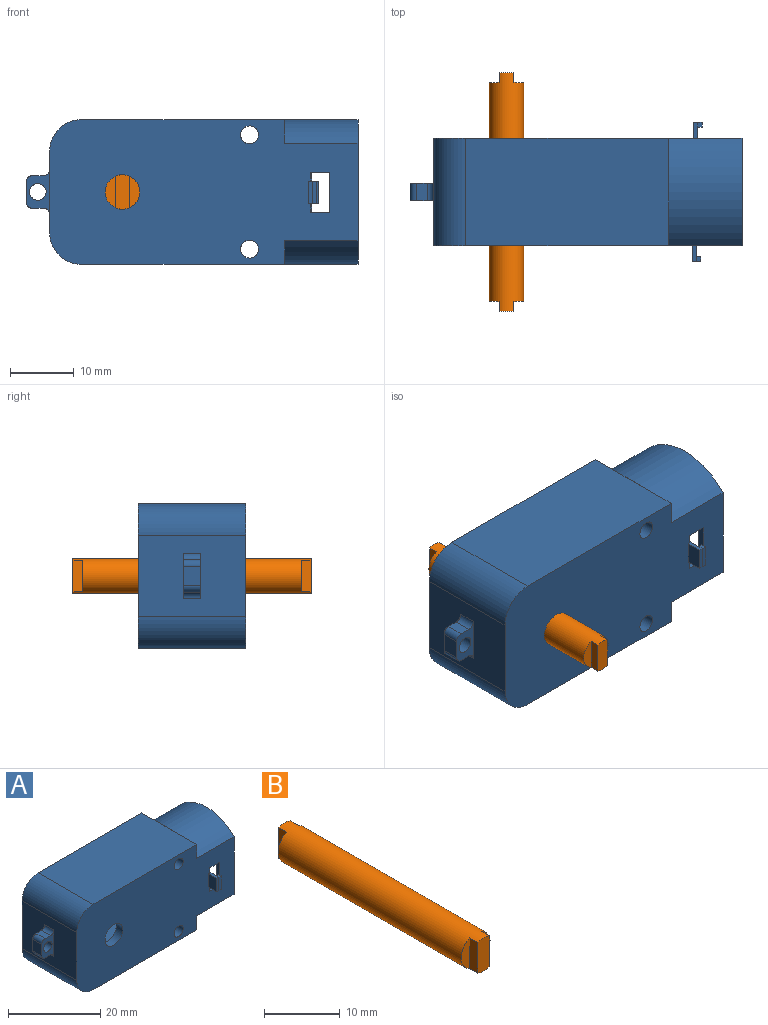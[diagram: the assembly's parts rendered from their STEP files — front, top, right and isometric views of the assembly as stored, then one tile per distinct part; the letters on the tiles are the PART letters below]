
ASSEMBLY  parts=2 mates=1
PART A: 73 faces, bbox 52x21.8x22.7 mm
  f0: plane 48.3x22.7mm, normal (0,-1,0), area 944.9mm2, adj f5,f8,f10,f11,f12,f13,f14,f15
  f1: plane 48.3x22.7mm, normal (0,1,0), area 944.9mm2, adj f6,f7,f8,f9,f10,f11,f12,f15
  f2: plane 14.47x11.5mm, normal (0,-1,0), area 148.7mm2, adj f4,f26,f27,f29,f38,f39,f40,f41
  f3: plane 14.47x11.5mm, normal (0,1,0), area 148.7mm2, adj f4,f26,f27,f29,f30,f31,f32,f33
  f4: plane 20.7x14.8mm, normal (1,0,0), area 254mm2, adj f2,f3,f24,f26,f27
  f5: plane 8.4x3.72mm, normal (1,0,0), area 9.6mm2, adj f0,f12,f28
  f6: plane 8.4x3.72mm, normal (1,0,0), area 9.6mm2, adj f1,f12,f28
  f7: plane 8.4x3.72mm, normal (1,0,0), area 9.6mm2, adj f1,f10,f25
  f8: cylinder r=1.4mm len=16.8mm, axis (0,1,0), area 81.1mm2, adj f0,f1,f16,f18,f22,f23
  f9: cylinder r=2.7mm len=5.4mm, axis (0,1,0), area 33.9mm2, adj f1,f23
  f10: plane 31.8x16.8mm, normal (0,0,1), area 534.2mm2, adj f0,f1,f7,f14,f67
  f11: plane 16.8x12.7mm, normal (-1,0,0), area 193.5mm2, adj f0,f1,f61,f63,f67,f68,f69,f70
  f12: plane 31.8x16.8mm, normal (0,0,-1), area 534.2mm2, adj f0,f1,f5,f6,f68
  f13: cylinder r=2.7mm len=5.4mm, axis (0,1,0), area 33.9mm2, adj f0,f22
  f14: plane 8.4x3.72mm, normal (1,0,0), area 9.6mm2, adj f0,f10,f25
  f15: cylinder r=1.4mm len=16.8mm, axis (0,1,0), area 81.1mm2, adj f0,f1,f17,f20,f22,f23
  f16: plane 27.96x12.8mm, normal (0,0,-1), area 357.9mm2, adj f8,f19,f22,f23
  f17: plane 27.96x12.8mm, normal (0,0,1), area 357.9mm2, adj f15,f19,f22,f23
  f18: plane 12.8x2.16mm, normal (0,0,-1), area 27.6mm2, adj f8,f21,f22,f23
  f19: plane 18.7x12.8mm, normal (1,0,0), area 239.4mm2, adj f16,f17,f22,f23
  f20: plane 12.8x2.16mm, normal (0,0,1), area 27.6mm2, adj f15,f21,f22,f23
  f21: plane 18.7x12.8mm, normal (-1,0,0), area 215.6mm2, adj f18,f20,f22,f23,f24
  f22: plane 32.8x18.7mm, normal (0,1,0), area 582.1mm2, adj f8,f13,f15,f16,f17,f18,f19,f20
  f23: plane 32.8x18.7mm, normal (0,-1,0), area 582.1mm2, adj f8,f9,f15,f16,f17,f18,f19,f20
  f24: cylinder r=2.75mm len=5.5mm, axis (1,0,0), area 34.6mm2, adj f4,f21
  f25: cylinder r=11.35mm len=16.8mm, axis (-1,0,0), area 217.5mm2, adj f0,f1,f7,f14,f29
  f26: cylinder r=10.35mm len=14.8mm, axis (-1,0,0), area 189.6mm2, adj f2,f3,f4,f29
  f27: cylinder r=10.35mm len=14.8mm, axis (-1,0,0), area 189.6mm2, adj f2,f3,f4,f29
  f28: cylinder r=11.35mm len=16.8mm, axis (-1,0,0), area 217.5mm2, adj f0,f1,f5,f6,f29
  f29: plane 22.7x16.8mm, normal (1,0,0), area 65.1mm2, adj f0,f1,f2,f3,f25,f26,f27,f28
  f30: plane 3.51x0.66mm, normal (0,0,1), area 1.9mm2, adj f0,f3,f31,f37,f54,f55,f59
  f31: plane 3.5x2.72mm, normal (1,0,0), area 9.5mm2, adj f3,f30,f32,f58
  f32: plane 3.51x0.66mm, normal (0,0,-1), area 1.9mm2, adj f0,f3,f31,f33,f54,f55,f57
  f33: plane 1.4x1mm, normal (1,0,0), area 1.4mm2, adj f0,f3,f32,f34
  f34: plane 3x1mm, normal (0,0,1), area 3mm2, adj f0,f3,f33,f35
  f35: plane 6.3x1mm, normal (-1,0,0), area 6.3mm2, adj f0,f3,f34,f36
  f36: plane 3x1mm, normal (0,0,-1), area 3mm2, adj f0,f3,f35,f37
  f37: plane 1.4x1mm, normal (1,0,0), area 1.4mm2, adj f0,f3,f30,f36
  f38: plane 3.51x0.65mm, normal (0,0,1), area 1.9mm2, adj f1,f2,f39,f45,f46,f47,f50
  f39: plane 1.4x1mm, normal (1,0,0), area 1.4mm2, adj f1,f2,f38,f40
  f40: plane 3x1mm, normal (0,0,-1), area 3mm2, adj f1,f2,f39,f41
  f41: plane 6.3x1mm, normal (-1,0,0), area 6.3mm2, adj f1,f2,f40,f42
  f42: plane 3x1mm, normal (0,0,1), area 3mm2, adj f1,f2,f41,f43
  f43: plane 1.4x1mm, normal (1,0,0), area 1.4mm2, adj f1,f2,f42,f44
  f44: plane 3.5x0.65mm, normal (0,0,-1), area 1.9mm2, adj f1,f2,f43,f45,f46,f47,f52
  f45: plane 3.5x2.72mm, normal (1,0,0), area 9.5mm2, adj f2,f38,f44,f51
  f46: plane 3.5x2.5mm, normal (-1,0,0), area 8.8mm2, adj f1,f38,f44,f47
  f47: plane 3.5x0.65mm, normal (0,1,0), area 2.3mm2, adj f38,f44,f46,f48
  f48: plane 3.5x0.01mm, normal (-1,0,0), area 0mm2, adj f47,f49
  f49: plane 3.5x0.68mm, normal (0,1,0), area 2.4mm2, adj f48,f50,f52,f53
  f50: plane 0.79x0.68mm, normal (0,0,1), area 0.5mm2, adj f38,f49,f51,f53
  f51: plane 3.5x0.68mm, normal (0,-1,0), area 2.4mm2, adj f45,f50,f52,f53
  f52: plane 0.79x0.68mm, normal (0,0,-1), area 0.5mm2, adj f44,f49,f51,f53
  f53: plane 3.5x0.78mm, normal (1,0,0), area 2.7mm2, adj f49,f50,f51,f52
  f54: plane 3.5x2.5mm, normal (-1,0,0), area 8.7mm2, adj f0,f30,f32,f55
  f55: plane 3.51x0.65mm, normal (0,-1,0), area 2.3mm2, adj f30,f32,f54,f56
  f56: plane 3.5x0.68mm, normal (0,-1,0), area 2.4mm2, adj f55,f57,f59,f60
  f57: plane 0.8x0.69mm, normal (0,0,-1), area 0.5mm2, adj f32,f56,f58,f60
  f58: plane 3.5x0.68mm, normal (0,1,0), area 2.4mm2, adj f31,f57,f59,f60
  f59: plane 0.8x0.69mm, normal (0,0,1), area 0.5mm2, adj f30,f56,f58,f60
  f60: plane 3.5x0.78mm, normal (1,0,0), area 2.7mm2, adj f56,f57,f58,f59
  f61: plane 7.1x3.71mm, normal (0,-1,0), area 13.6mm2, adj f11,f62,f64,f65,f66,f69,f70,f71
  f62: plane 2.8x1.71mm, normal (0,0,1), area 4.8mm2, adj f61,f63,f69,f71
  f63: plane 7.1x3.71mm, normal (0,1,0), area 13.6mm2, adj f11,f62,f64,f65,f66,f69,f70,f71
  f64: plane 2.8x1.71mm, normal (0,0,-1), area 4.8mm2, adj f61,f63,f70,f72
  f65: plane 3.1x2.8mm, normal (-1,0,0), area 8.7mm2, adj f61,f63,f71,f72
  f66: cylinder r=1.3mm len=2.8mm, axis (0,-1,0), area 22.9mm2, adj f61,f63
  f67: cylinder r=5mm len=16.8mm, axis (0,1,0), area 131.9mm2, adj f0,f1,f10,f11
  f68: cylinder r=5mm len=16.8mm, axis (0,-1,0), area 131.9mm2, adj f0,f1,f11,f12
  f69: cylinder r=1mm len=2.8mm, axis (0,1,0), area 4.4mm2, adj f11,f61,f62,f63
  f70: cylinder r=1mm len=2.8mm, axis (0,-1,0), area 4.4mm2, adj f11,f61,f63,f64
  f71: cylinder r=1mm len=2.8mm, axis (0,-1,0), area 4.4mm2, adj f61,f62,f63,f65
  f72: cylinder r=1mm len=2.8mm, axis (0,1,0), area 4.4mm2, adj f61,f63,f64,f65
PART B: 11 faces, bbox 5.4x37.3x5.4 mm
  f0: cylinder r=2.7mm len=37.3mm, axis (0,1,0), area 595mm2, adj f1,f2,f3,f4,f5,f6,f7,f8
  f1: plane 4.97x1.64mm, normal (0,-1,0), area 5.9mm2, adj f0,f3
  f2: plane 4.97x1.64mm, normal (0,1,0), area 5.9mm2, adj f0,f8
  f3: plane 4.97x1.5mm, normal (-1,0,0), area 7.4mm2, adj f0,f1,f9
  f4: plane 4.97x1.64mm, normal (0,-1,0), area 5.9mm2, adj f0,f6
  f5: plane 4.97x1.64mm, normal (0,1,0), area 5.9mm2, adj f0,f7
  f6: plane 4.97x1.5mm, normal (1,0,0), area 7.4mm2, adj f0,f4,f9
  f7: plane 4.97x1.5mm, normal (1,0,0), area 7.4mm2, adj f0,f5,f10
  f8: plane 4.97x1.5mm, normal (-1,0,0), area 7.4mm2, adj f0,f2,f10
  f9: plane 5.4x2.12mm, normal (0,-1,0), area 11.2mm2, adj f0,f3,f6
  f10: plane 5.4x2.12mm, normal (0,1,0), area 11.2mm2, adj f0,f7,f8
PLACE A t=(0.6,4.49,-1.73)mm
PLACE B t=(46.22,4.5,30.79)mm
MATE revolute B.f0 <-> A.f9  axis (0,1,0) through (21.31,4.5,9.62)mm
